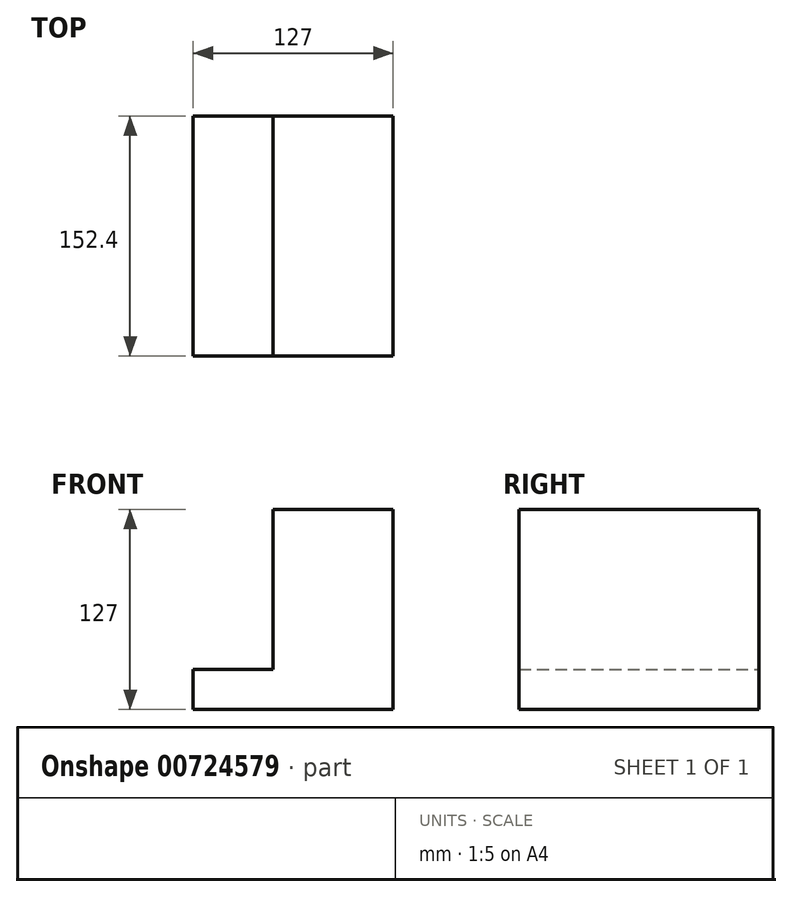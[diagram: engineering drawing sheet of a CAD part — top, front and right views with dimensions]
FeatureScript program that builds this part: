
annotation { "Feature Type Name" : "Feature", "Feature Type Description" : "" }
export const myFeature = defineFeature(function(context is Context, id is Id, definition is map)
    precondition{}
    {
        {
            var Q0;
            Q0=qCreatedBy(makeId("Front.planeOp"),FACE);
            var sketch = newSketch(context, id + "F0", { "sketchPlane" : qUnion([Q0])});
            skLineSegment(sketch, "E0", {"start": v(-76.2, -74.26) * mm, "end": v(-76.2, -48.86) * mm});
            skLineSegment(sketch, "E1", {"start": v(-76.2, -74.26) * mm, "end": v(50.8, -74.26) * mm});
            skLineSegment(sketch, "E2", {"start": v(50.8, -74.26) * mm, "end": v(50.8, 52.74) * mm});
            skLineSegment(sketch, "E3", {"start": v(50.8, 52.74) * mm, "end": v(-25.4, 52.74) * mm});
            skLineSegment(sketch, "E4", {"start": v(-25.4, 52.74) * mm, "end": v(-25.4, -48.86) * mm});
            skLineSegment(sketch, "E5", {"start": v(-25.4, -48.86) * mm, "end": v(-76.2, -48.86) * mm});
            skSolve(sketch);
        }
        {
            var Q0;
            Q0=makeQuery(id+"F0.imprint","IMPRINT",FACE,{"disambiguationData":[TD([[makeQuery(id+"F0.imprint","IMPRINT",EDGE,{"derivedFrom":sQuery(id+"F0.wireOp",EDGE,"E0")}),-1.0]])]});
            extrude(context, id + "F1", {"entities" : qUnion([Q0]), "depth" : 152.4 * mm, "offsetDistance" : 25.4 * mm});
        }
    });
